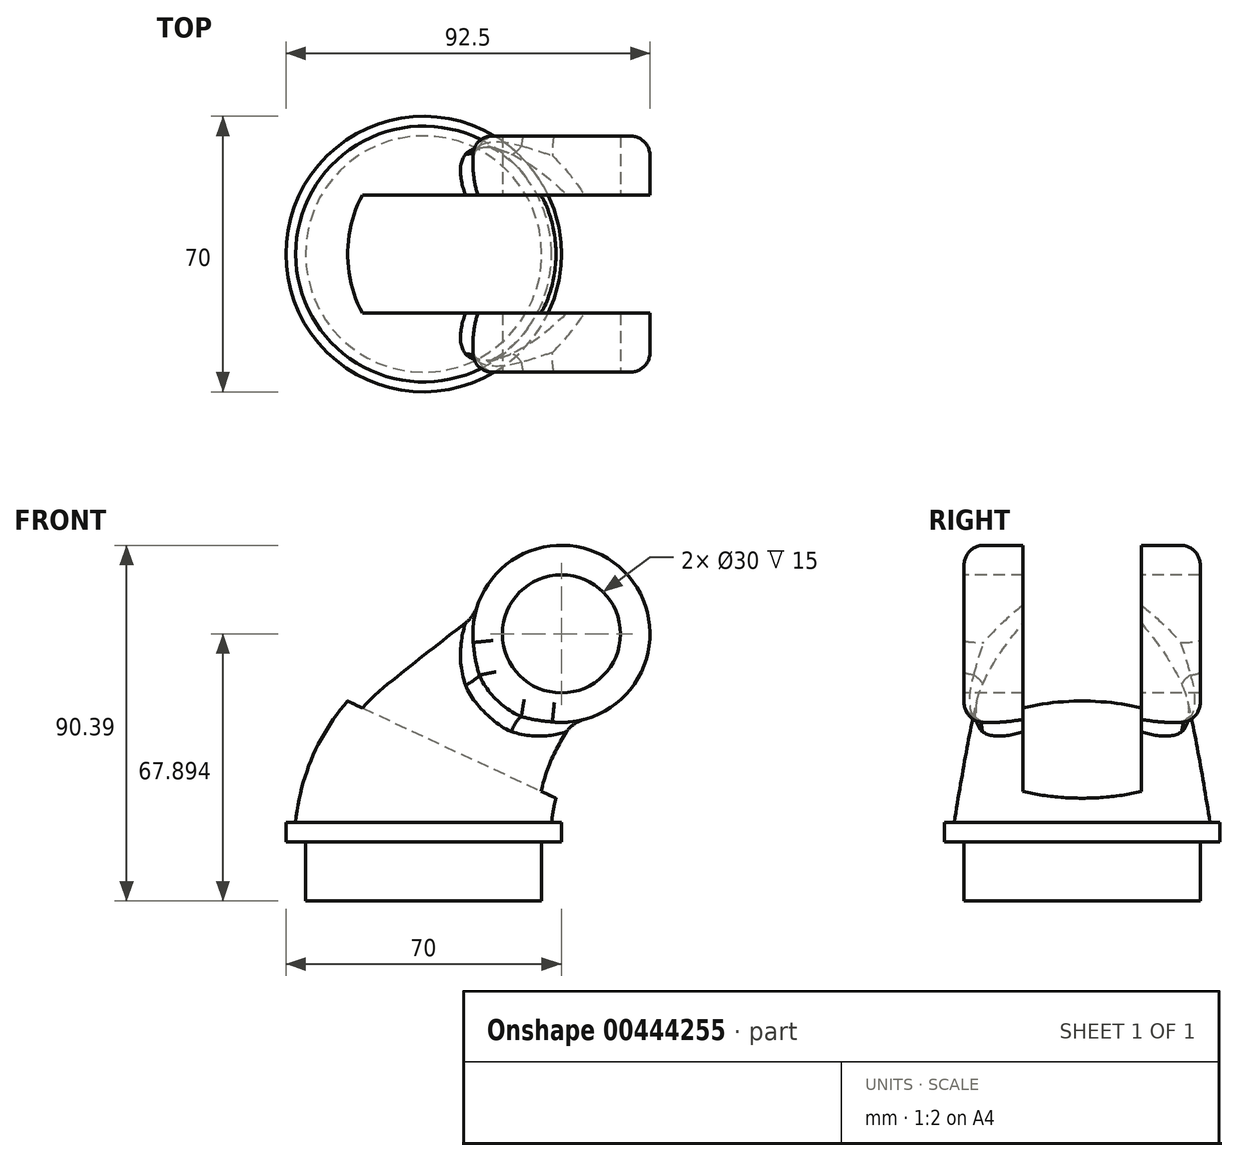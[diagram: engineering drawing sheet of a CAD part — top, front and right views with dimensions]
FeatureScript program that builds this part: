
annotation { "Feature Type Name" : "Feature", "Feature Type Description" : "" }
export const myFeature = defineFeature(function(context is Context, id is Id, definition is map)
    precondition{}
    {
        {
            var Q0;
            Q0=qCreatedBy(makeId("Top.planeOp"),FACE);
            var sketch = newSketch(context, id + "F0", { "sketchPlane" : qUnion([Q0])});
            skCircle(sketch, "E0", {"center": v(0, 0) * mm, "radius": 35 * mm});
            skSolve(sketch);
        }
        {
            var Q0;
            Q0 = qSketchRegion(id + "F0", true);
            extrude(context, id + "F1", {"entities" : qUnion([Q0]), "depth" : 5 * mm});
        }
        {
            var Q0;
            Q0=qCreatedBy(makeId("Front.planeOp"),FACE);
            var sketch = newSketch(context, id + "F2", { "sketchPlane" : qUnion([Q0])});
            skArc(sketch, "E1", {"start": v(17.6, 38.3) * mm, "mid": v(5.55, 23.37) * mm, "end": v(0, 5) * mm});
            skLineSegment(sketch, "E2", {"start": v(17.6, 38.3) * mm, "end": v(35, 52.9) * mm});
            skSolve(sketch);
        }
        {
            var Q0;
            Q0=sQuery(id+"F2.wireOp",EDGE,"E2");
            var Q1;
            Q1=sQuery(id+"F2.wireOp",VERTEX,"E2.end");
            cPlane(context, id + "F3", {"entities" : qUnion([Q0, Q1]), "cplaneType" : CPlaneType.LINE_POINT, "offset" : 25 * mm, "width" : 150 * mm, "height" : 150 * mm});
        }
        {
            var Q0;
            Q0=qCreatedBy(id+"F3.planeOp",FACE);
            var sketch = newSketch(context, id + "F4", { "sketchPlane" : qUnion([Q0])});
            skCircle(sketch, "E3", {"center": v(0, 18.02) * mm, "radius": 22.5 * mm});
            skSolve(sketch);
        }
        {
            var Q0;
            Q0=makeQuery(id+"F1.opExtrude","CAP_FACE",FACE,{"disambiguationData":[OSD([sQuery(id+"F0.wireOp",EDGE,"E0")])],"isStart":false});
            var sketch = newSketch(context, id + "F5", { "sketchPlane" : qUnion([Q0])});
            skCircle(sketch, "E4", {"center": v(0, 0) * mm, "radius": 32.5 * mm});
            skSolve(sketch);
        }
        {
            var Q0;
            Q0=qCreatedBy(makeId("Front.planeOp"),FACE);
            var sketch = newSketch(context, id + "F6", { "sketchPlane" : qUnion([Q0])});
            skArc(sketch, "E5", {"start": v(-13.25, 41.78) * mm, "mid": v(-26.5, 25.3) * mm, "end": v(-32.5, 5) * mm});
            skLineSegment(sketch, "E6", {"start": v(-13.25, 41.78) * mm, "end": v(20.54, 70.13) * mm});
            skSolve(sketch);
        }
        {
            var Q0;
            Q0=qCreatedBy(makeId("Front.planeOp"),FACE);
            var sketch = newSketch(context, id + "F7", { "sketchPlane" : qUnion([Q0])});
            skArc(sketch, "E7", {"start": v(48.46, 34.82) * mm, "mid": v(37.6, 21.45) * mm, "end": v(32.5, 5) * mm});
            skLineSegment(sketch, "E8", {"start": v(48.46, 34.82) * mm, "end": v(49.46, 35.66) * mm});
            skSolve(sketch);
        }
        {
            var Q1;
            Q1=makeQuery(id+"F5.imprint","IMPRINT",FACE,{"disambiguationData":[TD([[makeQuery(id+"F5.imprint","IMPRINT",EDGE,{"derivedFrom":sQuery(id+"F5.wireOp",EDGE,"E4")}),1.0]])]});
            var Q2;
            Q2=makeQuery(id+"F4.imprint","IMPRINT",FACE,{"disambiguationData":[TD([[makeQuery(id+"F4.imprint","IMPRINT",EDGE,{"derivedFrom":sQuery(id+"F4.wireOp",EDGE,"E3")}),1.0]])]});
            var Q3;
            Q3 = qConstructionFilter(qBodyType(qCreatedBy(id + "F7" ,EDGE), BodyType.WIRE), ConstructionObject.NO);
            var Q4;
            Q4 = qConstructionFilter(qBodyType(qCreatedBy(id + "F6" ,EDGE), BodyType.WIRE), ConstructionObject.NO);
            loft(context, id + "F8", {"operationType" : NewBodyOperationType.ADD, "addGuides" : true, "sheetProfilesArray" : [{ "sheetProfileEntities" : qUnion([Q1]) }, { "sheetProfileEntities" : qUnion([Q2]) }], "guidesArray" : [{ "guideEntities" : qUnion([Q3]), "guideDerivativeType" : LoftGuideDerivativeType.DEFAULT, "guideDerivativeMagnitude" : 1 }, { "guideEntities" : qUnion([Q4]), "guideDerivativeType" : LoftGuideDerivativeType.DEFAULT, "guideDerivativeMagnitude" : 1 }]});
        }
        {
            var Q0;
            Q0=qCreatedBy(makeId("Front.planeOp"),FACE);
            var sketch = newSketch(context, id + "F9", { "sketchPlane" : qUnion([Q0])});
            skCircle(sketch, "E9", {"center": v(35, 52.9) * mm, "radius": 22.5 * mm});
            skSolve(sketch);
        }
        {
            var Q0;
            Q0 = qSketchRegion(id + "F9", true);
            extrude(context, id + "F10", {"entities" : qUnion([Q0]), "operationType" : NewBodyOperationType.ADD, "endBound" : BoundingType.SYMMETRIC, "depth" : 60 * mm});
        }
        {
            var Q0;
            Q0=makeQuery(id+"F10.boolean.opBoolean","INTERSECT",EDGE,{"disambiguationData":[OD(1.0)],"derivedFrom":[makeQuery(id+"F8.opLoft","SWEPT_FACE",FACE,{"disambiguationData":[OSD([sQuery(id+"F4.wireOp",EDGE,"E3"),sQuery(id+"F5.wireOp",EDGE,"E4"),sQuery(id+"F6.wireOp",VERTEX,"E6.start"),sQuery(id+"F6.wireOp",EDGE,"E5"),sQuery(id+"F6.wireOp",EDGE,"E6"),sQuery(id+"F7.wireOp",VERTEX,"E8.start"),sQuery(id+"F7.wireOp",EDGE,"E7"),sQuery(id+"F7.wireOp",EDGE,"E8")])]}),makeQuery(id+"F10.opExtrude","SWEPT_FACE",FACE,{"disambiguationData":[OSD([sQuery(id+"F9.wireOp",EDGE,"E9")])]})]});
            var Q1;
            Q1=makeQuery(id+"F10.boolean.opBoolean","INTERSECT",EDGE,{"disambiguationData":[OD(0.0)],"derivedFrom":[makeQuery(id+"F8.opLoft","SWEPT_FACE",FACE,{"disambiguationData":[OSD([sQuery(id+"F4.wireOp",EDGE,"E3"),sQuery(id+"F5.wireOp",EDGE,"E4"),sQuery(id+"F6.wireOp",VERTEX,"E6.start"),sQuery(id+"F6.wireOp",EDGE,"E5"),sQuery(id+"F6.wireOp",EDGE,"E6"),sQuery(id+"F7.wireOp",VERTEX,"E8.start"),sQuery(id+"F7.wireOp",EDGE,"E7"),sQuery(id+"F7.wireOp",EDGE,"E8")])]}),makeQuery(id+"F10.opExtrude","SWEPT_FACE",FACE,{"disambiguationData":[OSD([sQuery(id+"F9.wireOp",EDGE,"E9")])]})]});
            fillet(context, id + "F11", {"entities" : qUnion([Q0, Q1]), "radius" : 5 * mm, "tangentPropagation" : true, "allowEdgeOverflow" : false});
        }
        {
            var Q0;
            Q0=makeQuery(id+"F10.opExtrude","CAP_EDGE",EDGE,{"disambiguationData":[OSD([sQuery(id+"F9.wireOp",EDGE,"E9")])],"isStart":true});
            var Q1;
            Q1=makeQuery(id+"F10.opExtrude","CAP_EDGE",EDGE,{"disambiguationData":[OSD([sQuery(id+"F9.wireOp",EDGE,"E9")])],"isStart":false});
            fillet(context, id + "F12", {"entities" : qUnion([Q0, Q1]), "radius" : 5 * mm, "tangentPropagation" : true, "allowEdgeOverflow" : false});
        }
        {
            var Q0;
            Q0=makeQuery(id+"F10.opExtrude","CAP_FACE",FACE,{"disambiguationData":[OSD([sQuery(id+"F9.wireOp",EDGE,"E9")])],"isStart":false});
            var sketch = newSketch(context, id + "F13", { "sketchPlane" : qUnion([Q0])});
            skCircle(sketch, "E10", {"center": v(35, 52.9) * mm, "radius": 15 * mm});
            skSolve(sketch);
        }
        {
            var Q0;
            Q0 = qSketchRegion(id + "F13", true);
            extrude(context, id + "F14", {"entities" : qUnion([Q0]), "operationType" : NewBodyOperationType.REMOVE, "endBound" : BoundingType.THROUGH_ALL, "oppositeDirection" : true, "depth" : 25 * mm});
        }
        {
            var Q0;
            Q0=qCreatedBy(makeId("Front.planeOp"),FACE);
            var sketch = newSketch(context, id + "F15", { "sketchPlane" : qUnion([Q0])});
            skLineSegment(sketch, "E11", {"start": v(-104.18, 75.4) * mm, "end": v(57.5, 0) * mm});
            skLineSegment(sketch, "E12", {"start": v(57.5, 75.4) * mm, "end": v(57.5, 0) * mm});
            skLineSegment(sketch, "E13", {"start": v(-104.18, 75.4) * mm, "end": v(57.5, 75.4) * mm});
            skSolve(sketch);
        }
        {
            var Q0;
            Q0 = qSketchRegion(id + "F15", true);
            extrude(context, id + "F16", {"entities" : qUnion([Q0]), "operationType" : NewBodyOperationType.REMOVE, "endBound" : BoundingType.SYMMETRIC, "oppositeDirection" : true, "depth" : 30 * mm});
        }
        {
            var Q0;
            Q0=qCreatedBy(makeId("Front.planeOp"),FACE);
            var sketch = newSketch(context, id + "F17", { "sketchPlane" : qUnion([Q0])});
            skLineSegment(sketch, "E14.bottom", {"start": v(0, 0) * mm, "end": v(-30, 0) * mm});
            skLineSegment(sketch, "E14.top", {"start": v(0, -15) * mm, "end": v(-30, -15) * mm});
            skLineSegment(sketch, "E14.left", {"start": v(0, 0) * mm, "end": v(0, -15) * mm});
            skLineSegment(sketch, "E14.right", {"start": v(-30, 0) * mm, "end": v(-30, -15) * mm});
            skSolve(sketch);
        }
        {
            var Q0;
            Q0=makeQuery(id+"F17.imprint","IMPRINT",FACE,{"disambiguationData":[TD([[makeQuery(id+"F17.imprint","IMPRINT",EDGE,{"derivedFrom":sQuery(id+"F17.wireOp",EDGE,"E14.bottom")}),1.0]])]});
            var Q1;
            Q1=sQuery(id+"F17.wireOp",EDGE,"E14.left");
            revolve(context, id + "F18", {"operationType" : NewBodyOperationType.ADD, "entities" : qUnion([Q0]), "axis" : qUnion([Q1]), "revolveType" : RevolveType.FULL});
        }
    });
